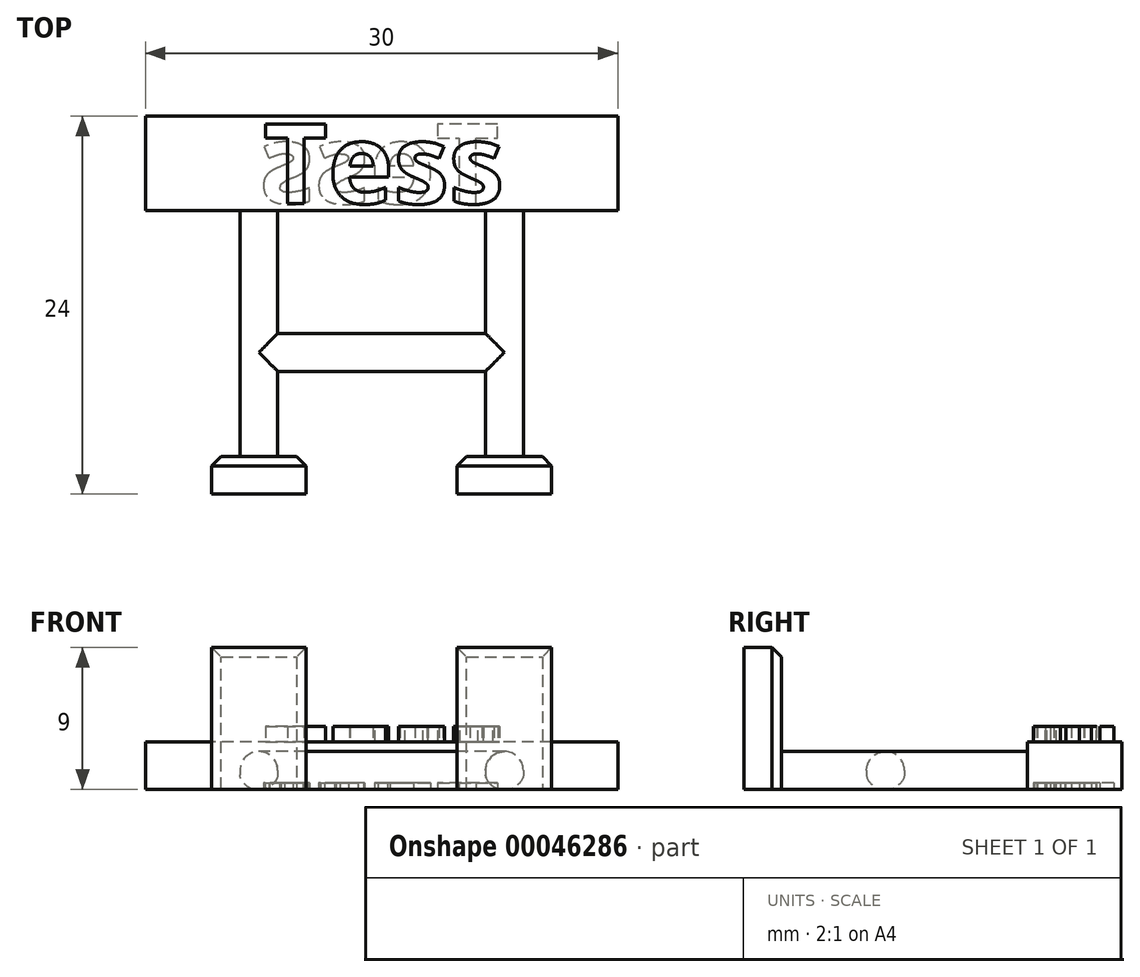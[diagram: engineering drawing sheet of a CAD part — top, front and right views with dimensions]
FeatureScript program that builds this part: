
annotation { "Feature Type Name" : "Feature", "Feature Type Description" : "" }
export const myFeature = defineFeature(function(context is Context, id is Id, definition is map)
    precondition{}
    {
        {
            assignVariable(context, id + "F0", {"name" : "hurdle_width", "anyValue" : 30});
        }
        {
            var Q0;
            Q0=qCreatedBy(makeId("Top.planeOp"),FACE);
            var sketch = newSketch(context, id + "F1", { "sketchPlane" : qUnion([Q0])});
            skLineSegment(sketch, "E0.rect.bottom", {"start": v(15, -3) * mm, "end": v(-15, -3) * mm});
            skLineSegment(sketch, "E0.rect.top", {"start": v(15, 3) * mm, "end": v(-15, 3) * mm});
            skLineSegment(sketch, "E0.rect.left", {"start": v(15, -3) * mm, "end": v(15, 3) * mm});
            skLineSegment(sketch, "E0.rect.right", {"start": v(-15, -3) * mm, "end": v(-15, 3) * mm});
            skPoint(sketch, "E0.rect.middle", {"position": v(0, 0) * mm});
            skLineSegment(sketch, "E1", {"start": v(0, 0) * mm, "end": v(0, -21) * mm, "construction": true});
            skLineSegment(sketch, "E2.bottom", {"start": v(-9, -3) * mm, "end": v(-6.6, -3) * mm, "construction": true});
            skLineSegment(sketch, "E2.left", {"start": v(-9, -3) * mm, "end": v(-9, -18.6) * mm});
            skLineSegment(sketch, "E2.right", {"start": v(-6.6, -3) * mm, "end": v(-6.6, -18.6) * mm});
            skLineSegment(sketch, "E3.bottom", {"start": v(-10.8, -18.6) * mm, "end": v(-4.8, -18.6) * mm});
            skLineSegment(sketch, "E3.top", {"start": v(-10.8, -21) * mm, "end": v(-4.8, -21) * mm});
            skLineSegment(sketch, "E3.left", {"start": v(-10.8, -18.6) * mm, "end": v(-10.8, -21) * mm});
            skLineSegment(sketch, "E3.right", {"start": v(-4.8, -18.6) * mm, "end": v(-4.8, -21) * mm});
            skPoint(sketch, "E4", {"position": v(-7.8, -18.6) * mm});
            skLineSegment(sketch, "E5", {"start": v(-9, -18.6) * mm, "end": v(-6.6, -18.6) * mm});
            skLineSegment(sketch, "E6.MirrorCS", {"start": v(6.6, -3) * mm, "end": v(6.6, -18.6) * mm});
            skLineSegment(sketch, "E7.MirrorCS", {"start": v(9, -3) * mm, "end": v(9, -18.6) * mm});
            skLineSegment(sketch, "E8.MirrorCS", {"start": v(10.8, -21) * mm, "end": v(4.8, -21) * mm});
            skLineSegment(sketch, "E9.MirrorCS", {"start": v(4.8, -18.6) * mm, "end": v(4.8, -21) * mm});
            skLineSegment(sketch, "E10.MirrorCS", {"start": v(10.8, -18.6) * mm, "end": v(10.8, -21) * mm});
            skLineSegment(sketch, "E11.MirrorCS", {"start": v(10.8, -18.6) * mm, "end": v(4.8, -18.6) * mm});
            skLineSegment(sketch, "E12.bottom", {"start": v(-6.6, -10.8) * mm, "end": v(6.6, -10.8) * mm});
            skLineSegment(sketch, "E12.top", {"start": v(-6.6, -13.2) * mm, "end": v(6.6, -13.2) * mm});
            skLineSegment(sketch, "E12.left", {"start": v(-6.6, -10.8) * mm, "end": v(-6.6, -13.2) * mm});
            skLineSegment(sketch, "E12.right", {"start": v(6.6, -10.8) * mm, "end": v(6.6, -13.2) * mm});
            skSolve(sketch);
        }
        {
            var Q0;
            Q0=makeQuery(id+"F1.imprint","IMPRINT",FACE,{"disambiguationData":[TD([[makeQuery(id+"F1.imprint","IMPRINT",EDGE,{"derivedFrom":sQuery(id+"F1.wireOp",EDGE,"E0.rect.top")}),1.0]])]});
            extrude(context, id + "F2", {"entities" : qUnion([Q0]), "depth" : (getVariable(context, 'hurdle_width') / 10) * mm});
        }
        {
            var Q0;
            Q0=makeQuery(id+"F2.opExtrude","CAP_FACE",FACE,{"disambiguationData":[OSD([sQuery(id+"F1.wireOp",EDGE,"E0.rect.bottom"),sQuery(id+"F1.wireOp",EDGE,"E0.rect.top"),sQuery(id+"F1.wireOp",EDGE,"E0.rect.left"),sQuery(id+"F1.wireOp",EDGE,"E0.rect.right")])],"isStart":true});
            var sketch = newSketch(context, id + "F3", { "sketchPlane" : qUnion([Q0])});
            skText(sketch, "E13", { "text": "Tess", "fontName": "OpenSans-Bold.ttf"});
            skLineSegment(sketch, "E14", {"start": v(0, -2.54) * mm, "end": v(0, -3) * mm, "construction": true});
            skLineSegment(sketch, "E15", {"start": v(0, 2.54) * mm, "end": v(0, 3) * mm, "construction": true});
            const initialGuessF3  = {"E13": [0.0075, 0.00254, -1, 0, 0.00508]};
            skSetInitialGuess(sketch, initialGuessF3);
            skSolve(sketch);
        }
        {
            var Q0;
            Q0=makeQuery(id+"F1.imprint","IMPRINT",FACE,{"disambiguationData":[TD([[makeQuery(id+"F1.imprint","IMPRINT",EDGE,{"derivedFrom":sQuery(id+"F1.wireOp",EDGE,"E3.top")}),1.0]])]});
            var Q1;
            Q1=makeQuery(id+"F1.imprint","IMPRINT",FACE,{"disambiguationData":[TD([[makeQuery(id+"F1.imprint","IMPRINT",EDGE,{"derivedFrom":sQuery(id+"F1.wireOp",EDGE,"E8.MirrorCS")}),-1.0]])]});
            extrude(context, id + "F4", {"entities" : qUnion([Q0, Q1]), "depth" : (0.3 * getVariable(context, 'hurdle_width')) * mm});
        }
        {
            var Q0;
            {var subQ2=sQuery(id+"F1.wireOp",EDGE,"E2.left");Q0=makeQuery(id+"F1.imprint","IMPRINT",FACE,{"disambiguationData":[TD([[makeQuery(id+"F1.imprint","IMPRINT",EDGE,{"derivedFrom":subQ2}),1.0]])]});}
            var Q1;
            Q1=makeQuery(id+"F1.imprint","IMPRINT",FACE,{"disambiguationData":[TD([[makeQuery(id+"F1.imprint","IMPRINT",EDGE,{"derivedFrom":sQuery(id+"F1.wireOp",EDGE,"E12.bottom")}),-1.0]])]});
            var Q2;
            {var subQ2=sQuery(id+"F1.wireOp",EDGE,"E7.MirrorCS");Q2=makeQuery(id+"F1.imprint","IMPRINT",FACE,{"disambiguationData":[TD([[makeQuery(id+"F1.imprint","IMPRINT",EDGE,{"derivedFrom":subQ2}),-1.0]])]});}
            extrude(context, id + "F5", {"entities" : qUnion([Q0, Q1, Q2]), "operationType" : NewBodyOperationType.ADD, "depth" : (0.08 * getVariable(context, 'hurdle_width')) * mm});
        }
        {
            var Q0;
            {var subQ0=sQuery(id+"F1.wireOp",EDGE,"E2.right");Q0=makeQuery(id+"F5.opExtrude","CAP_EDGE",EDGE,{"disambiguationData":[OSD([subQ0]),TDD([makeQuery(id+"F1.imprint","IMPRINT",EDGE,{"disambiguationData":[TD([[makeQuery(id+"F1.imprint","INTERSECT",VERTEX,{"derivedFrom":[sQuery(id+"F1.wireOp",EDGE,"E0.rect.bottom"),subQ0]}),-1.0]])],"derivedFrom":subQ0})])],"isStart":false});}
            var Q1;
            Q1=makeQuery(id+"F5.opExtrude","CAP_EDGE",EDGE,{"disambiguationData":[OSD([sQuery(id+"F1.wireOp",EDGE,"E2.left")])],"isStart":false});
            var Q2;
            {var subQ0=sQuery(id+"F1.wireOp",EDGE,"E2.right");Q2=makeQuery(id+"F5.opExtrude","CAP_EDGE",EDGE,{"disambiguationData":[OSD([subQ0]),TDD([makeQuery(id+"F1.imprint","IMPRINT",EDGE,{"disambiguationData":[TD([[makeQuery(id+"F1.imprint","INTERSECT",VERTEX,{"derivedFrom":[subQ0,sQuery(id+"F1.wireOp",EDGE,"E3.bottom"),sQuery(id+"F1.wireOp",EDGE,"E5")]}),1.0]])],"derivedFrom":subQ0})])],"isStart":false});}
            var Q3;
            Q3=makeQuery(id+"F5.opExtrude","CAP_EDGE",EDGE,{"disambiguationData":[OSD([sQuery(id+"F1.wireOp",EDGE,"E12.top")])],"isStart":false});
            var Q4;
            Q4=makeQuery(id+"F5.opExtrude","CAP_EDGE",EDGE,{"disambiguationData":[OSD([sQuery(id+"F1.wireOp",EDGE,"E12.bottom")])],"isStart":false});
            var Q5;
            Q5=makeQuery(id+"F5.opExtrude","CAP_EDGE",EDGE,{"disambiguationData":[OSD([sQuery(id+"F1.wireOp",EDGE,"E7.MirrorCS")])],"isStart":false});
            var Q6;
            {var subQ0=sQuery(id+"F1.wireOp",EDGE,"E6.MirrorCS");Q6=makeQuery(id+"F5.opExtrude","CAP_EDGE",EDGE,{"disambiguationData":[OSD([subQ0]),TDD([makeQuery(id+"F1.imprint","IMPRINT",EDGE,{"disambiguationData":[TD([[makeQuery(id+"F1.imprint","INTERSECT",VERTEX,{"derivedFrom":[subQ0,sQuery(id+"F1.wireOp",EDGE,"E11.MirrorCS")]}),1.0]])],"derivedFrom":subQ0})])],"isStart":false});}
            var Q7;
            {var subQ0=sQuery(id+"F1.wireOp",EDGE,"E6.MirrorCS");Q7=makeQuery(id+"F5.opExtrude","CAP_EDGE",EDGE,{"disambiguationData":[OSD([subQ0]),TDD([makeQuery(id+"F1.imprint","IMPRINT",EDGE,{"disambiguationData":[TD([[makeQuery(id+"F1.imprint","INTERSECT",VERTEX,{"derivedFrom":[sQuery(id+"F1.wireOp",EDGE,"E0.rect.bottom"),subQ0]}),-1.0]])],"derivedFrom":subQ0})])],"isStart":false});}
            fillet(context, id + "F6", {"entities" : qUnion([Q0, Q1, Q2, Q3, Q4, Q5, Q6, Q7]), "radius" : (0.04 * getVariable(context, 'hurdle_width')) * mm, "tangentPropagation" : true, "allowEdgeOverflow" : false});
        }
        {
            var Q0;
            Q0=makeQuery(id+"F4.opExtrude","SWEPT_EDGE",EDGE,{"disambiguationData":[OSD([sQuery(id+"F1.wireOp",EDGE,"E3.bottom"),sQuery(id+"F1.wireOp",EDGE,"E3.left")])]});
            var Q1;
            Q1=makeQuery(id+"F4.opExtrude","CAP_EDGE",EDGE,{"disambiguationData":[OSD([sQuery(id+"F1.wireOp",EDGE,"E3.bottom"),sQuery(id+"F1.wireOp",EDGE,"E5")])],"isStart":false});
            var Q2;
            Q2=makeQuery(id+"F4.opExtrude","SWEPT_EDGE",EDGE,{"disambiguationData":[OSD([sQuery(id+"F1.wireOp",EDGE,"E3.bottom"),sQuery(id+"F1.wireOp",EDGE,"E3.right")])]});
            var Q3;
            Q3=makeQuery(id+"F4.opExtrude","SWEPT_EDGE",EDGE,{"disambiguationData":[OSD([sQuery(id+"F1.wireOp",EDGE,"E9.MirrorCS"),sQuery(id+"F1.wireOp",EDGE,"E11.MirrorCS")])]});
            var Q4;
            Q4=makeQuery(id+"F4.opExtrude","CAP_EDGE",EDGE,{"disambiguationData":[OSD([sQuery(id+"F1.wireOp",EDGE,"E11.MirrorCS")])],"isStart":false});
            var Q5;
            Q5=makeQuery(id+"F4.opExtrude","SWEPT_EDGE",EDGE,{"disambiguationData":[OSD([sQuery(id+"F1.wireOp",EDGE,"E10.MirrorCS"),sQuery(id+"F1.wireOp",EDGE,"E11.MirrorCS")])]});
            chamfer(context, id + "F7", {"entities" : qUnion([Q0, Q1, Q2, Q3, Q4, Q5]), "width" : (getVariable(context, 'hurdle_width') / 50) * mm, "tangentPropagation" : true});
        }
        {
            var Q0;
            Q0=makeQuery(id+"F5.opExtrude","CAP_EDGE",EDGE,{"disambiguationData":[OSD([sQuery(id+"F1.wireOp",EDGE,"E2.left")])],"isStart":true});
            var Q1;
            {var subQ0=sQuery(id+"F1.wireOp",EDGE,"E2.right");Q1=makeQuery(id+"F5.opExtrude","CAP_EDGE",EDGE,{"disambiguationData":[OSD([subQ0]),TDD([makeQuery(id+"F1.imprint","IMPRINT",EDGE,{"disambiguationData":[TD([[makeQuery(id+"F1.imprint","INTERSECT",VERTEX,{"derivedFrom":[subQ0,sQuery(id+"F1.wireOp",EDGE,"E3.bottom"),sQuery(id+"F1.wireOp",EDGE,"E5")]}),1.0]])],"derivedFrom":subQ0})])],"isStart":true});}
            var Q2;
            {var subQ0=sQuery(id+"F1.wireOp",EDGE,"E2.right");Q2=makeQuery(id+"F5.opExtrude","CAP_EDGE",EDGE,{"disambiguationData":[OSD([subQ0]),TDD([makeQuery(id+"F1.imprint","IMPRINT",EDGE,{"disambiguationData":[TD([[makeQuery(id+"F1.imprint","INTERSECT",VERTEX,{"derivedFrom":[sQuery(id+"F1.wireOp",EDGE,"E0.rect.bottom"),subQ0]}),-1.0]])],"derivedFrom":subQ0})])],"isStart":true});}
            var Q3;
            Q3=makeQuery(id+"F5.opExtrude","CAP_EDGE",EDGE,{"disambiguationData":[OSD([sQuery(id+"F1.wireOp",EDGE,"E12.bottom")])],"isStart":true});
            var Q4;
            Q4=makeQuery(id+"F5.opExtrude","CAP_EDGE",EDGE,{"disambiguationData":[OSD([sQuery(id+"F1.wireOp",EDGE,"E12.top")])],"isStart":true});
            var Q5;
            {var subQ0=sQuery(id+"F1.wireOp",EDGE,"E6.MirrorCS");Q5=makeQuery(id+"F5.opExtrude","CAP_EDGE",EDGE,{"disambiguationData":[OSD([subQ0]),TDD([makeQuery(id+"F1.imprint","IMPRINT",EDGE,{"disambiguationData":[TD([[makeQuery(id+"F1.imprint","INTERSECT",VERTEX,{"derivedFrom":[subQ0,sQuery(id+"F1.wireOp",EDGE,"E11.MirrorCS")]}),1.0]])],"derivedFrom":subQ0})])],"isStart":true});}
            var Q6;
            {var subQ0=sQuery(id+"F1.wireOp",EDGE,"E6.MirrorCS");Q6=makeQuery(id+"F5.opExtrude","CAP_EDGE",EDGE,{"disambiguationData":[OSD([subQ0]),TDD([makeQuery(id+"F1.imprint","IMPRINT",EDGE,{"disambiguationData":[TD([[makeQuery(id+"F1.imprint","INTERSECT",VERTEX,{"derivedFrom":[sQuery(id+"F1.wireOp",EDGE,"E0.rect.bottom"),subQ0]}),-1.0]])],"derivedFrom":subQ0})])],"isStart":true});}
            var Q7;
            Q7=makeQuery(id+"F5.opExtrude","CAP_EDGE",EDGE,{"disambiguationData":[OSD([sQuery(id+"F1.wireOp",EDGE,"E7.MirrorCS")])],"isStart":true});
            fillet(context, id + "F8", {"entities" : qUnion([Q0, Q1, Q2, Q3, Q4, Q5, Q6, Q7]), "radius" : (1.5 * getVariable(context, 'hurdle_width') / 50) * mm, "tangentPropagation" : true, "rho" : 0.3, "crossSection" : FilletCrossSection.CONIC, "allowEdgeOverflow" : false});
        }
        {
            var Q0;
            Q0=makeQuery(id+"F2.opExtrude","CAP_FACE",FACE,{"disambiguationData":[OSD([sQuery(id+"F1.wireOp",EDGE,"E0.rect.bottom"),sQuery(id+"F1.wireOp",EDGE,"E0.rect.top"),sQuery(id+"F1.wireOp",EDGE,"E0.rect.left"),sQuery(id+"F1.wireOp",EDGE,"E0.rect.right")])],"isStart":false});
            var sketch = newSketch(context, id + "F9", { "sketchPlane" : qUnion([Q0])});
            skText(sketch, "E16", { "text": "Tess", "fontName": "OpenSans-Bold.ttf"});
            skLineSegment(sketch, "E17", {"start": v(0, 2.54) * mm, "end": v(0, 3) * mm, "construction": true});
            skLineSegment(sketch, "E18", {"start": v(0, -2.54) * mm, "end": v(0, -3) * mm, "construction": true});
            const initialGuessF9  = {"E16": [-0.0075, -0.00254, 1, 0, 0.00508]};
            skSetInitialGuess(sketch, initialGuessF9);
            skSolve(sketch);
        }
        {
            var Q0;
            Q0 = qSketchRegion(id + "F9", true);
            extrude(context, id + "F10", {"entities" : qUnion([Q0]), "operationType" : NewBodyOperationType.ADD, "depth" : 1 * mm});
        }
        {
            var Q0;
            Q0 = qSketchRegion(id + "F3", true);
            extrude(context, id + "F11", {"entities" : qUnion([Q0]), "operationType" : NewBodyOperationType.REMOVE, "oppositeDirection" : true, "depth" : 0.4 * mm});
        }
    });
